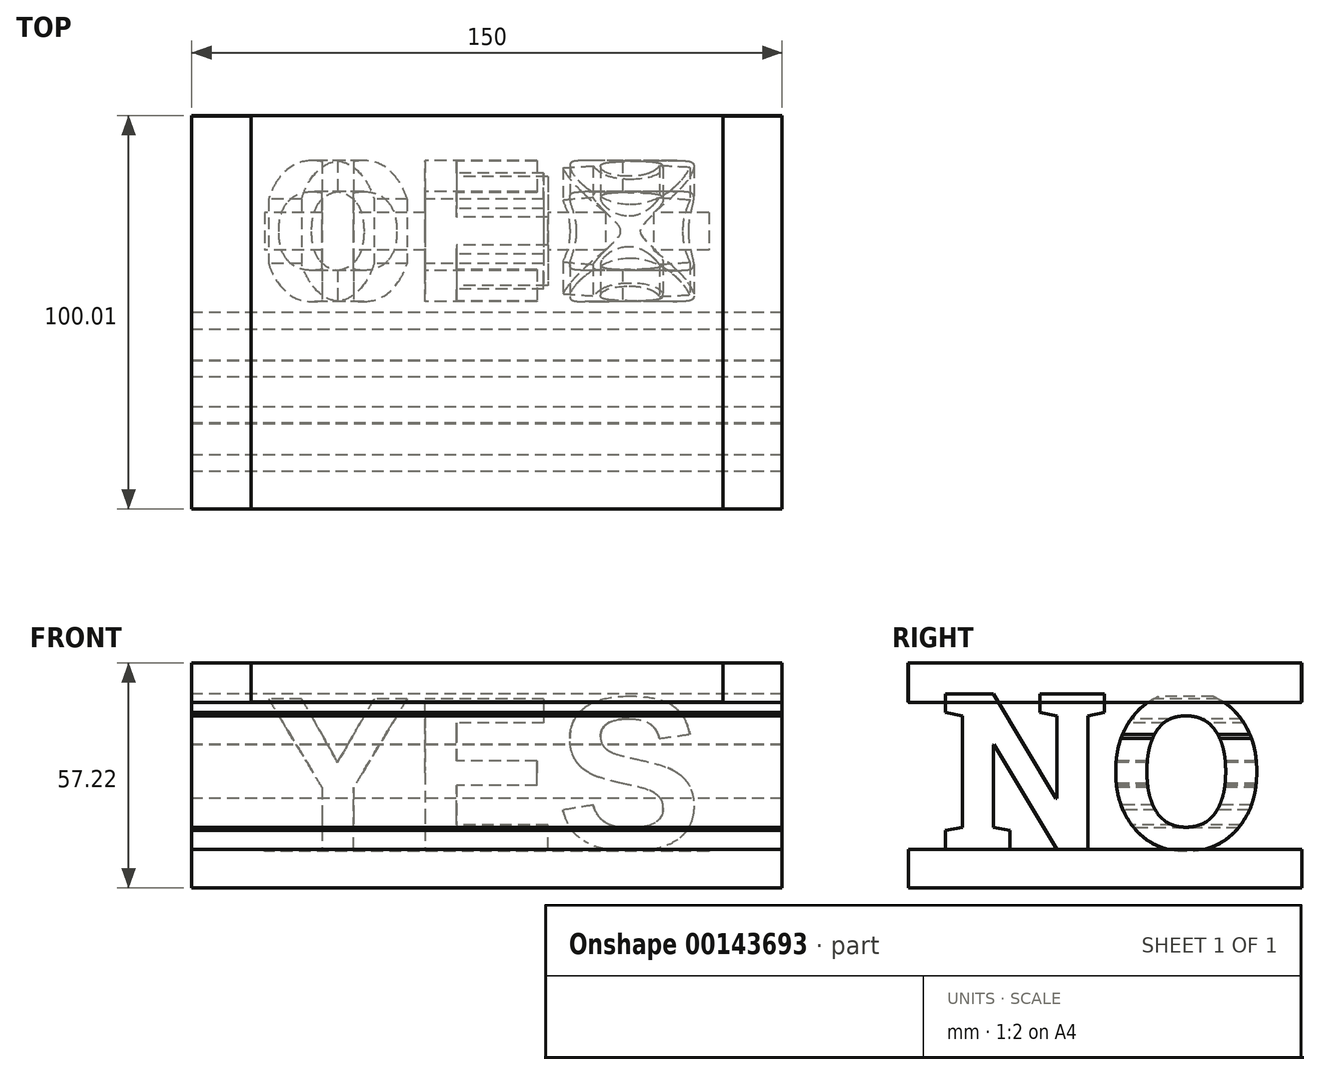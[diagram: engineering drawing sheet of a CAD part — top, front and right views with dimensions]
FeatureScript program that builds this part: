
annotation { "Feature Type Name" : "Feature", "Feature Type Description" : "" }
export const myFeature = defineFeature(function(context is Context, id is Id, definition is map)
    precondition{}
    {
        {
            var Q0;
            Q0=qCreatedBy(makeId("Front.planeOp"),FACE);
            var sketch = newSketch(context, id + "F0", { "sketchPlane" : qUnion([Q0])});
            skText(sketch, "E0", { "text": "YES", "fontName": "Arimo-Bold.ttf"});
            skLineSegment(sketch, "E1.bottom", {"start": v(-56.43, 0) * mm, "end": v(56.43, 0) * mm});
            skLineSegment(sketch, "E1.top", {"start": v(-56.43, -10) * mm, "end": v(56.43, -10) * mm});
            skLineSegment(sketch, "E1.left", {"start": v(-56.43, 0) * mm, "end": v(-56.43, -10) * mm});
            skLineSegment(sketch, "E1.right", {"start": v(56.43, 0) * mm, "end": v(56.43, -10) * mm});
            const initialGuessF0  = {"E0": [-0.05643, 0, 1, 0, 0.04]};
            skSetInitialGuess(sketch, initialGuessF0);
            skSolve(sketch);
        }
        {
            var Q0;
            Q0 = qSketchRegion(id + "F0", true);
            extrude(context, id + "F1", {"entities" : qUnion([Q0]), "oppositeDirection" : true, "depth" : 100 * mm, "symmetric" : true});
        }
        {
            var Q0;
            Q0=qCreatedBy(makeId("Right.planeOp"),FACE);
            var sketch = newSketch(context, id + "F2", { "sketchPlane" : qUnion([Q0])});
            skText(sketch, "E2", { "text": "NO", "fontName": "RobotoSlab-Bold.ttf"});
            const initialGuessF2  = {"E2": [-0.04197, 0, 1, 0, 0.04]};
            skSetInitialGuess(sketch, initialGuessF2);
            skSolve(sketch);
        }
        {
            var Q0;
            Q0 = qSketchRegion(id + "F2", true);
            extrude(context, id + "F3", {"entities" : qUnion([Q0]), "depth" : 150 * mm, "symmetric" : true});
        }
        {
            var Q0;
            Q0=qCreatedBy(makeId("Front.planeOp"),FACE);
            var sketch = newSketch(context, id + "F4", { "sketchPlane" : qUnion([Q0])});
            skLineSegment(sketch, "E3.bottom", {"start": v(59.92, 37.4) * mm, "end": v(-59.9, 37.4) * mm});
            skLineSegment(sketch, "E3.top", {"start": v(59.92, 47.4) * mm, "end": v(-59.9, 47.4) * mm});
            skLineSegment(sketch, "E3.left", {"start": v(59.92, 37.4) * mm, "end": v(59.92, 47.4) * mm});
            skLineSegment(sketch, "E3.right", {"start": v(-59.9, 37.4) * mm, "end": v(-59.9, 47.4) * mm});
            skSolve(sketch);
        }
        {
            var Q0;
            Q0 = qSketchRegion(id + "F4", true);
            extrude(context, id + "F5", {"entities" : qUnion([Q0]), "depth" : 100 * mm, "symmetric" : true});
        }
        {
            var Q0;
            Q0=qCreatedBy(makeId("Right.planeOp"),FACE);
            var sketch = newSketch(context, id + "F6", { "sketchPlane" : qUnion([Q0])});
            skLineSegment(sketch, "E4.bottom", {"start": v(-49.93, 0) * mm, "end": v(50.01, 0) * mm});
            skLineSegment(sketch, "E4.top", {"start": v(-49.93, -9.83) * mm, "end": v(50.01, -9.83) * mm});
            skLineSegment(sketch, "E4.left", {"start": v(-49.93, 0) * mm, "end": v(-49.93, -9.83) * mm});
            skLineSegment(sketch, "E4.right", {"start": v(50.01, 0) * mm, "end": v(50.01, -9.83) * mm});
            skLineSegment(sketch, "E5.bottom", {"start": v(-49.96, 47.35) * mm, "end": v(49.9, 47.35) * mm});
            skLineSegment(sketch, "E5.top", {"start": v(-49.96, 37.25) * mm, "end": v(49.9, 37.25) * mm});
            skLineSegment(sketch, "E5.left", {"start": v(-49.96, 47.35) * mm, "end": v(-49.96, 37.25) * mm});
            skLineSegment(sketch, "E5.right", {"start": v(49.9, 47.35) * mm, "end": v(49.9, 37.25) * mm});
            skSolve(sketch);
        }
        {
            var Q0;
            Q0 = qSketchRegion(id + "F6", true);
            extrude(context, id + "F7", {"entities" : qUnion([Q0]), "depth" : 150 * mm, "symmetric" : true});
        }
        {
            var Q0;
            Q0=makeQuery(id+"F1.opExtrude","SWEPT_BODY",BODY,{"disambiguationData":[OSD([sQuery(id+"F0.wireOp",EDGE,"E0.sketch_text.stroke-0"),sQuery(id+"F0.wireOp",EDGE,"E0.sketch_text.stroke-2"),sQuery(id+"F0.wireOp",EDGE,"E0.sketch_text.stroke-3"),sQuery(id+"F0.wireOp",EDGE,"E0.sketch_text.stroke-4"),sQuery(id+"F0.wireOp",EDGE,"E0.sketch_text.stroke-5"),sQuery(id+"F0.wireOp",EDGE,"E0.sketch_text.stroke-6"),sQuery(id+"F0.wireOp",EDGE,"E0.sketch_text.stroke-7"),sQuery(id+"F0.wireOp",EDGE,"E0.sketch_text.stroke-8"),sQuery(id+"F0.wireOp",EDGE,"E0.sketch_text.stroke-9"),sQuery(id+"F0.wireOp",EDGE,"E0.sketch_text.stroke-10"),sQuery(id+"F0.wireOp",EDGE,"E0.sketch_text.stroke-11"),sQuery(id+"F0.wireOp",EDGE,"E0.sketch_text.stroke-12"),sQuery(id+"F0.wireOp",EDGE,"E0.sketch_text.stroke-13"),sQuery(id+"F0.wireOp",EDGE,"E0.sketch_text.stroke-14"),sQuery(id+"F0.wireOp",EDGE,"E0.sketch_text.stroke-15"),sQuery(id+"F0.wireOp",EDGE,"E0.sketch_text.stroke-16"),sQuery(id+"F0.wireOp",EDGE,"E0.sketch_text.stroke-17"),sQuery(id+"F0.wireOp",EDGE,"E0.sketch_text.stroke-18"),sQuery(id+"F0.wireOp",EDGE,"E0.sketch_text.stroke-19"),sQuery(id+"F0.wireOp",EDGE,"E0.sketch_text.stroke-21"),sQuery(id+"F0.wireOp",EDGE,"E0.sketch_text.stroke-22"),sQuery(id+"F0.wireOp",EDGE,"E0.sketch_text.stroke-23"),sQuery(id+"F0.wireOp",EDGE,"E0.sketch_text.stroke-24"),sQuery(id+"F0.wireOp",EDGE,"E0.sketch_text.stroke-25"),sQuery(id+"F0.wireOp",EDGE,"E0.sketch_text.stroke-26"),sQuery(id+"F0.wireOp",EDGE,"E0.sketch_text.stroke-27"),sQuery(id+"F0.wireOp",EDGE,"E0.sketch_text.stroke-28"),sQuery(id+"F0.wireOp",EDGE,"E0.sketch_text.stroke-29"),sQuery(id+"F0.wireOp",EDGE,"E0.sketch_text.stroke-30"),sQuery(id+"F0.wireOp",EDGE,"E0.sketch_text.stroke-31"),sQuery(id+"F0.wireOp",EDGE,"E0.sketch_text.stroke-32"),sQuery(id+"F0.wireOp",EDGE,"E0.sketch_text.stroke-33"),sQuery(id+"F0.wireOp",EDGE,"E0.sketch_text.stroke-34"),sQuery(id+"F0.wireOp",EDGE,"E0.sketch_text.stroke-35"),sQuery(id+"F0.wireOp",EDGE,"E0.sketch_text.stroke-36"),sQuery(id+"F0.wireOp",EDGE,"E0.sketch_text.stroke-37"),sQuery(id+"F0.wireOp",EDGE,"E0.sketch_text.stroke-38"),sQuery(id+"F0.wireOp",EDGE,"E0.sketch_text.stroke-39"),sQuery(id+"F0.wireOp",EDGE,"E0.sketch_text.stroke-40"),sQuery(id+"F0.wireOp",EDGE,"E0.sketch_text.stroke-41"),sQuery(id+"F0.wireOp",EDGE,"E0.sketch_text.stroke-42"),sQuery(id+"F0.wireOp",EDGE,"E0.sketch_text.stroke-43"),sQuery(id+"F0.wireOp",EDGE,"E0.sketch_text.stroke-44"),sQuery(id+"F0.wireOp",EDGE,"E0.sketch_text.stroke-45"),sQuery(id+"F0.wireOp",EDGE,"E0.sketch_text.stroke-46"),sQuery(id+"F0.wireOp",EDGE,"E0.sketch_text.stroke-47"),sQuery(id+"F0.wireOp",EDGE,"E0.sketch_text.stroke-48"),sQuery(id+"F0.wireOp",EDGE,"E0.sketch_text.stroke-49"),sQuery(id+"F0.wireOp",EDGE,"E0.sketch_text.stroke-50"),sQuery(id+"F0.wireOp",EDGE,"E0.sketch_text.stroke-51"),sQuery(id+"F0.wireOp",EDGE,"E1.bottom"),sQuery(id+"F0.wireOp",EDGE,"E1.top"),sQuery(id+"F0.wireOp",EDGE,"E1.left"),sQuery(id+"F0.wireOp",EDGE,"E1.right")])]});
            var Q1;
            Q1=makeQuery(id+"F3.opExtrude","SWEPT_BODY",BODY,{"disambiguationData":[OSD([sQuery(id+"F2.wireOp",EDGE,"E2.sketch_text.stroke-24"),sQuery(id+"F2.wireOp",EDGE,"E2.sketch_text.stroke-25"),sQuery(id+"F2.wireOp",EDGE,"E2.sketch_text.stroke-26"),sQuery(id+"F2.wireOp",EDGE,"E2.sketch_text.stroke-27"),sQuery(id+"F2.wireOp",EDGE,"E2.sketch_text.stroke-28"),sQuery(id+"F2.wireOp",EDGE,"E2.sketch_text.stroke-29"),sQuery(id+"F2.wireOp",EDGE,"E2.sketch_text.stroke-30"),sQuery(id+"F2.wireOp",EDGE,"E2.sketch_text.stroke-31"),sQuery(id+"F2.wireOp",EDGE,"E2.sketch_text.stroke-32"),sQuery(id+"F2.wireOp",EDGE,"E2.sketch_text.stroke-33"),sQuery(id+"F2.wireOp",EDGE,"E2.sketch_text.stroke-34"),sQuery(id+"F2.wireOp",EDGE,"E2.sketch_text.stroke-35"),sQuery(id+"F2.wireOp",EDGE,"E2.sketch_text.stroke-36"),sQuery(id+"F2.wireOp",EDGE,"E2.sketch_text.stroke-37"),sQuery(id+"F2.wireOp",EDGE,"E2.sketch_text.stroke-38"),sQuery(id+"F2.wireOp",EDGE,"E2.sketch_text.stroke-39"),sQuery(id+"F2.wireOp",EDGE,"E2.sketch_text.stroke-40"),sQuery(id+"F2.wireOp",EDGE,"E2.sketch_text.stroke-41"),sQuery(id+"F2.wireOp",EDGE,"E2.sketch_text.stroke-42"),sQuery(id+"F2.wireOp",EDGE,"E2.sketch_text.stroke-43")])]});
            booleanBodies(context, id + "F8", {"operationType" : BooleanOperationType.INTERSECTION, "tools" : qUnion([Q0, Q1])});
        }
    });
